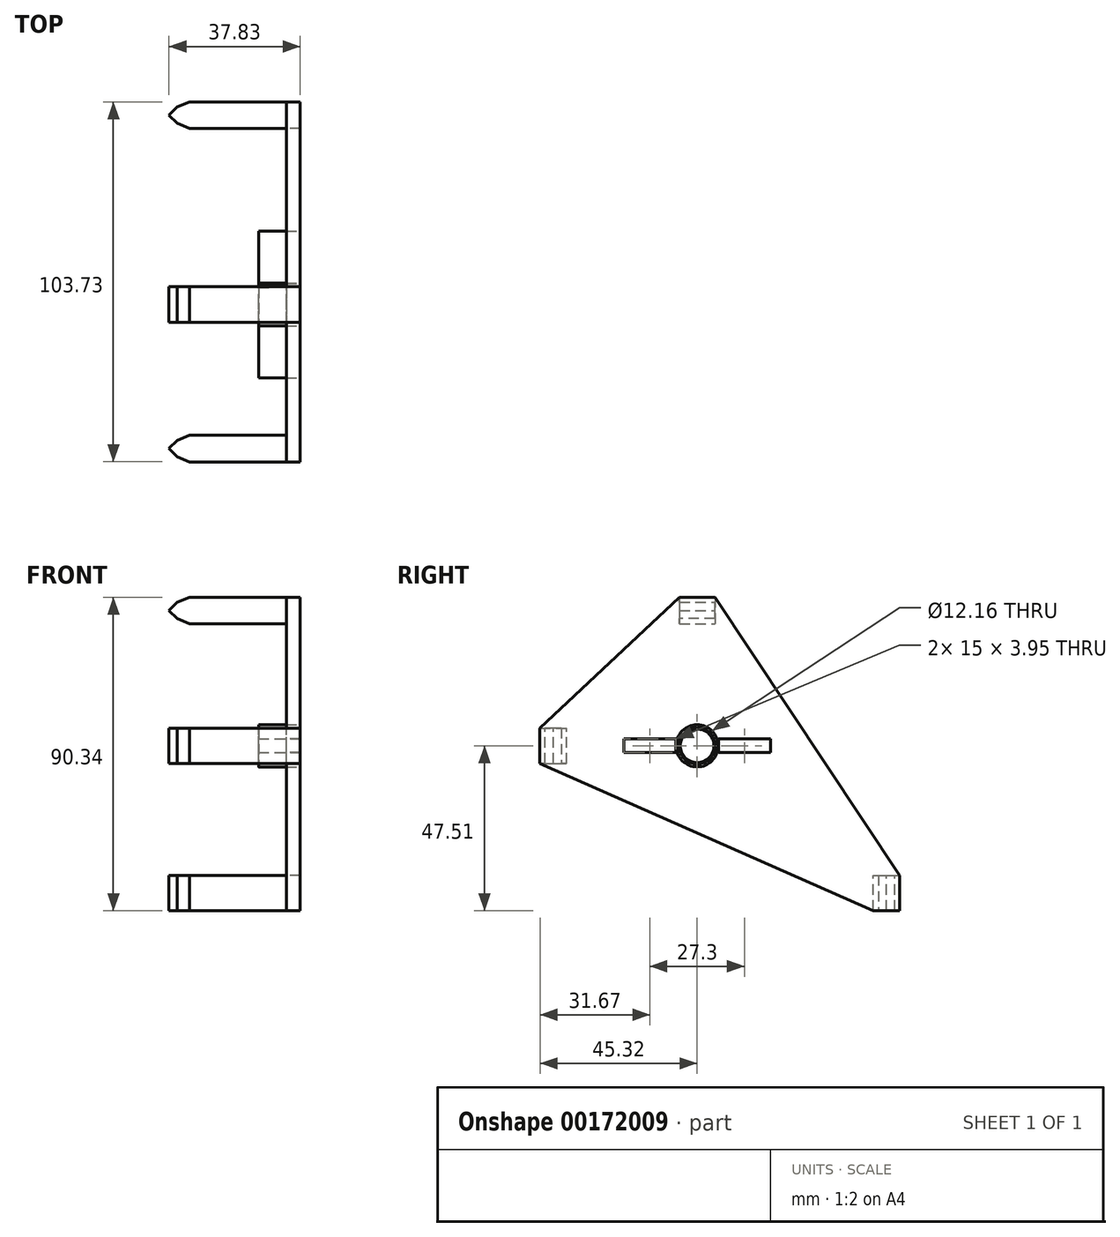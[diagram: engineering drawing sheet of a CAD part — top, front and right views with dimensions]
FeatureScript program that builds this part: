
annotation { "Feature Type Name" : "Feature", "Feature Type Description" : "" }
export const myFeature = defineFeature(function(context is Context, id is Id, definition is map)
    precondition{}
    {
        {
            var Q0;
            Q0=qCreatedBy(makeId("Right.planeOp"),FACE);
            var sketch = newSketch(context, id + "F0", { "sketchPlane" : qUnion([Q0])});
            skCircle(sketch, "E0", {"center": v(0, 0) * mm, "radius": 4.25 * mm});
            skLineSegment(sketch, "E1.bottom", {"start": v(21.15, -1.97) * mm, "end": v(6.15, -1.97) * mm});
            skLineSegment(sketch, "E1.top", {"start": v(21.15, 1.98) * mm, "end": v(6.15, 1.98) * mm});
            skLineSegment(sketch, "E1.left", {"start": v(21.15, -1.97) * mm, "end": v(21.15, 1.98) * mm});
            skLineSegment(sketch, "E1.right", {"start": v(6.15, -1.97) * mm, "end": v(6.15, 1.98) * mm});
            skPoint(sketch, "E1.middle", {"position": v(13.65, 0) * mm});
            skPoint(sketch, "E2.MirrorP", {"position": v(-13.65, 0) * mm});
            skLineSegment(sketch, "E3.MirrorCS", {"start": v(-21.15, -1.97) * mm, "end": v(-21.15, 1.98) * mm});
            skLineSegment(sketch, "E4.MirrorCS", {"start": v(-21.15, 1.98) * mm, "end": v(-6.15, 1.98) * mm});
            skLineSegment(sketch, "E5.MirrorCS", {"start": v(-21.15, -1.97) * mm, "end": v(-6.15, -1.97) * mm});
            skLineSegment(sketch, "E6.MirrorCS", {"start": v(-6.15, -1.97) * mm, "end": v(-6.15, 1.98) * mm});
            skCircle(sketch, "E7", {"center": v(0, 0) * mm, "radius": 6.08 * mm});
            skLineSegment(sketch, "E8.bottom", {"start": v(-5.1, 42.83) * mm, "end": v(5.1, 42.83) * mm});
            skLineSegment(sketch, "E8.top", {"start": v(-5.1, 35.17) * mm, "end": v(5.1, 35.17) * mm});
            skLineSegment(sketch, "E8.left", {"start": v(-5.1, 42.83) * mm, "end": v(-5.1, 35.17) * mm});
            skLineSegment(sketch, "E8.right", {"start": v(5.1, 42.83) * mm, "end": v(5.1, 35.17) * mm});
            skPoint(sketch, "E8.middle", {"position": v(0, 39) * mm});
            skLineSegment(sketch, "E9.bottom", {"start": v(-45.33, -5.1) * mm, "end": v(-37.68, -5.1) * mm});
            skLineSegment(sketch, "E9.top", {"start": v(-45.33, 5.1) * mm, "end": v(-37.68, 5.1) * mm});
            skLineSegment(sketch, "E9.left", {"start": v(-45.33, -5.1) * mm, "end": v(-45.33, 5.1) * mm});
            skLineSegment(sketch, "E9.right", {"start": v(-37.68, -5.1) * mm, "end": v(-37.68, 5.1) * mm});
            skPoint(sketch, "E9.middle", {"position": v(-41.5, 0) * mm});
            skLineSegment(sketch, "E10.bottom", {"start": v(50.76, -47.5) * mm, "end": v(58.4, -47.5) * mm});
            skLineSegment(sketch, "E10.top", {"start": v(50.76, -37.3) * mm, "end": v(58.4, -37.3) * mm});
            skLineSegment(sketch, "E10.left", {"start": v(50.76, -47.5) * mm, "end": v(50.76, -37.3) * mm});
            skLineSegment(sketch, "E10.right", {"start": v(58.4, -47.5) * mm, "end": v(58.4, -37.3) * mm});
            skPoint(sketch, "E10.middle", {"position": v(54.58, -42.4) * mm});
            skLineSegment(sketch, "E11", {"start": v(-5.1, 42.83) * mm, "end": v(-45.33, 5.1) * mm});
            skLineSegment(sketch, "E12", {"start": v(58.4, -37.3) * mm, "end": v(5.1, 42.82) * mm});
            skLineSegment(sketch, "E13", {"start": v(50.76, -47.5) * mm, "end": v(-45.33, -5.1) * mm});
            skLineSegment(sketch, "E14", {"start": v(0, 4.25) * mm, "end": v(0, 6.08) * mm});
            skLineSegment(sketch, "E15", {"start": v(4.25, 0) * mm, "end": v(6.08, 0) * mm});
            skLineSegment(sketch, "E16", {"start": v(0, -4.25) * mm, "end": v(0, -6.08) * mm});
            skLineSegment(sketch, "E17", {"start": v(-4.25, 0) * mm, "end": v(-6.08, 0) * mm});
            skSolve(sketch);
        }
        {
            var Q0;
            Q0 = qSketchRegion(id + "F0", true);
            extrude(context, id + "F1", {"entities" : qUnion([Q0]), "depth" : 4 * mm});
        }
        {
            var Q0;
            Q0=makeQuery(id+"F0.imprint","IMPRINT",FACE,{"disambiguationData":[TD([[makeQuery(id+"F0.imprint","IMPRINT",EDGE,{"derivedFrom":sQuery(id+"F0.wireOp",EDGE,"E3.MirrorCS")}),-1.0]])]});
            var Q1;
            Q1=makeQuery(id+"F0.imprint","IMPRINT",FACE,{"disambiguationData":[TD([[makeQuery(id+"F0.imprint","IMPRINT",EDGE,{"derivedFrom":sQuery(id+"F0.wireOp",EDGE,"E1.bottom")}),-1.0]])]});
            var Q2;
            Q2=makeQuery(id+"F0.imprint","IMPRINT",FACE,{"disambiguationData":[TD([[makeQuery(id+"F0.imprint","IMPRINT",EDGE,{"derivedFrom":sQuery(id+"F0.wireOp",EDGE,"E0")}),-1.0]])]});
            extrude(context, id + "F2", {"entities" : qUnion([Q0, Q1, Q2]), "oppositeDirection" : true, "depth" : 8 * mm, "hasSecondDirection" : true, "secondDirectionOppositeDirection" : false, "secondDirectionDepth" : 4 * mm});
        }
        {
            var Q0;
            Q0=makeQuery(id+"F0.imprint","IMPRINT",FACE,{"disambiguationData":[TD([[makeQuery(id+"F0.imprint","IMPRINT",EDGE,{"derivedFrom":sQuery(id+"F0.wireOp",EDGE,"E8.bottom")}),-1.0]])]});
            var Q1;
            Q1=makeQuery(id+"F0.imprint","IMPRINT",FACE,{"disambiguationData":[TD([[makeQuery(id+"F0.imprint","IMPRINT",EDGE,{"derivedFrom":sQuery(id+"F0.wireOp",EDGE,"E9.bottom")}),1.0]])]});
            var Q2;
            Q2=makeQuery(id+"F0.imprint","IMPRINT",FACE,{"disambiguationData":[TD([[makeQuery(id+"F0.imprint","IMPRINT",EDGE,{"derivedFrom":sQuery(id+"F0.wireOp",EDGE,"E10.bottom")}),1.0]])]});
            extrude(context, id + "F3", {"entities" : qUnion([Q0, Q1, Q2]), "operationType" : NewBodyOperationType.ADD, "oppositeDirection" : true, "depth" : 34 * mm});
        }
        {
            var Q0;
            Q0=makeQuery(id+"F3.opExtrude","CAP_EDGE",EDGE,{"disambiguationData":[OSD([sQuery(id+"F0.wireOp",EDGE,"E10.right")])],"isStart":false});
            var Q1;
            Q1=makeQuery(id+"F3.opExtrude","CAP_EDGE",EDGE,{"disambiguationData":[OSD([sQuery(id+"F0.wireOp",EDGE,"E10.left")])],"isStart":false});
            var Q2;
            Q2=makeQuery(id+"F3.opExtrude","CAP_EDGE",EDGE,{"disambiguationData":[OSD([sQuery(id+"F0.wireOp",EDGE,"E9.right")])],"isStart":false});
            var Q3;
            Q3=makeQuery(id+"F3.opExtrude","CAP_EDGE",EDGE,{"disambiguationData":[OSD([sQuery(id+"F0.wireOp",EDGE,"E9.left")])],"isStart":false});
            var Q4;
            Q4=makeQuery(id+"F3.opExtrude","CAP_EDGE",EDGE,{"disambiguationData":[OSD([sQuery(id+"F0.wireOp",EDGE,"E8.top")])],"isStart":false});
            var Q5;
            Q5=makeQuery(id+"F3.opExtrude","CAP_EDGE",EDGE,{"disambiguationData":[OSD([sQuery(id+"F0.wireOp",EDGE,"E8.bottom")])],"isStart":false});
            chamfer(context, id + "F4", {"entities" : qUnion([Q0, Q1, Q2, Q3, Q4, Q5]), "width" : 4 * mm, "tangentPropagation" : true});
        }
        {
            var Q0;
            Q0=makeQuery(id+"F2.opExtrude","CAP_EDGE",EDGE,{"disambiguationData":[OSD([sQuery(id+"F0.wireOp",EDGE,"E0")])],"isStart":true});
            chamfer(context, id + "F5", {"entities" : qUnion([Q0]), "chamferType" : ChamferType.OFFSET_ANGLE, "width" : 1 * mm, "oppositeDirection" : true, "angle" : 88 * degree, "tangentPropagation" : true});
        }
        {
            var Q0;
            {var subQ0=sQuery(id+"F0.wireOp",EDGE,"E8.bottom");Q0=makeQuery(id+"F4.opChamfer","BLEND_EDGE",EDGE,{"blendedFrom":[makeQuery(id+"F3.opExtrude","CAP_EDGE",EDGE,{"disambiguationData":[OSD([subQ0])],"isStart":false}),makeQuery(id+"F3.boolean.opBoolean","MERGE",FACE,{"derivedFrom":[makeQuery(id+"F1.opExtrude","SWEPT_FACE",FACE,{"disambiguationData":[OSD([subQ0])]}),makeQuery(id+"F3.opExtrude","SWEPT_FACE",FACE,{"disambiguationData":[OSD([subQ0])]})]})],"blendedInto":[makeQuery(id+"F3.boolean.opBoolean","MERGE",FACE,{"derivedFrom":[makeQuery(id+"F1.opExtrude","SWEPT_FACE",FACE,{"disambiguationData":[OSD([subQ0])]}),makeQuery(id+"F3.opExtrude","SWEPT_FACE",FACE,{"disambiguationData":[OSD([subQ0])]})]})]});}
            var Q1;
            {var subQ0=sQuery(id+"F0.wireOp",EDGE,"E8.top");Q1=makeQuery(id+"F4.opChamfer","BLEND_EDGE",EDGE,{"blendedFrom":[makeQuery(id+"F3.opExtrude","CAP_EDGE",EDGE,{"disambiguationData":[OSD([subQ0])],"isStart":false}),makeQuery(id+"F3.opExtrude","SWEPT_FACE",FACE,{"disambiguationData":[OSD([subQ0])]})],"blendedInto":[makeQuery(id+"F3.opExtrude","SWEPT_FACE",FACE,{"disambiguationData":[OSD([subQ0])]})]});}
            var Q2;
            {var subQ0=sQuery(id+"F0.wireOp",EDGE,"E9.right");Q2=makeQuery(id+"F4.opChamfer","BLEND_EDGE",EDGE,{"blendedFrom":[makeQuery(id+"F3.opExtrude","CAP_EDGE",EDGE,{"disambiguationData":[OSD([subQ0])],"isStart":false}),makeQuery(id+"F3.opExtrude","SWEPT_FACE",FACE,{"disambiguationData":[OSD([subQ0])]})],"blendedInto":[makeQuery(id+"F3.opExtrude","SWEPT_FACE",FACE,{"disambiguationData":[OSD([subQ0])]})]});}
            var Q3;
            {var subQ0=sQuery(id+"F0.wireOp",EDGE,"E10.right");Q3=makeQuery(id+"F4.opChamfer","BLEND_EDGE",EDGE,{"blendedFrom":[makeQuery(id+"F3.opExtrude","CAP_EDGE",EDGE,{"disambiguationData":[OSD([subQ0])],"isStart":false}),makeQuery(id+"F3.boolean.opBoolean","MERGE",FACE,{"derivedFrom":[makeQuery(id+"F1.opExtrude","SWEPT_FACE",FACE,{"disambiguationData":[OSD([subQ0])]}),makeQuery(id+"F3.opExtrude","SWEPT_FACE",FACE,{"disambiguationData":[OSD([subQ0])]})]})],"blendedInto":[makeQuery(id+"F3.boolean.opBoolean","MERGE",FACE,{"derivedFrom":[makeQuery(id+"F1.opExtrude","SWEPT_FACE",FACE,{"disambiguationData":[OSD([subQ0])]}),makeQuery(id+"F3.opExtrude","SWEPT_FACE",FACE,{"disambiguationData":[OSD([subQ0])]})]})]});}
            var Q4;
            {var subQ0=sQuery(id+"F0.wireOp",EDGE,"E9.left");Q4=makeQuery(id+"F4.opChamfer","BLEND_EDGE",EDGE,{"blendedFrom":[makeQuery(id+"F3.opExtrude","CAP_EDGE",EDGE,{"disambiguationData":[OSD([subQ0])],"isStart":false}),makeQuery(id+"F3.boolean.opBoolean","MERGE",FACE,{"derivedFrom":[makeQuery(id+"F1.opExtrude","SWEPT_FACE",FACE,{"disambiguationData":[OSD([subQ0])]}),makeQuery(id+"F3.opExtrude","SWEPT_FACE",FACE,{"disambiguationData":[OSD([subQ0])]})]})],"blendedInto":[makeQuery(id+"F3.boolean.opBoolean","MERGE",FACE,{"derivedFrom":[makeQuery(id+"F1.opExtrude","SWEPT_FACE",FACE,{"disambiguationData":[OSD([subQ0])]}),makeQuery(id+"F3.opExtrude","SWEPT_FACE",FACE,{"disambiguationData":[OSD([subQ0])]})]})]});}
            var Q5;
            {var subQ0=sQuery(id+"F0.wireOp",EDGE,"E10.left");Q5=makeQuery(id+"F4.opChamfer","BLEND_EDGE",EDGE,{"blendedFrom":[makeQuery(id+"F3.opExtrude","CAP_EDGE",EDGE,{"disambiguationData":[OSD([subQ0])],"isStart":false}),makeQuery(id+"F3.opExtrude","SWEPT_FACE",FACE,{"disambiguationData":[OSD([subQ0])]})],"blendedInto":[makeQuery(id+"F3.opExtrude","SWEPT_FACE",FACE,{"disambiguationData":[OSD([subQ0])]})]});}
            chamfer(context, id + "F6", {"entities" : qUnion([Q0, Q1, Q2, Q3, Q4, Q5]), "width" : 5 * mm, "tangentPropagation" : true});
        }
    });
